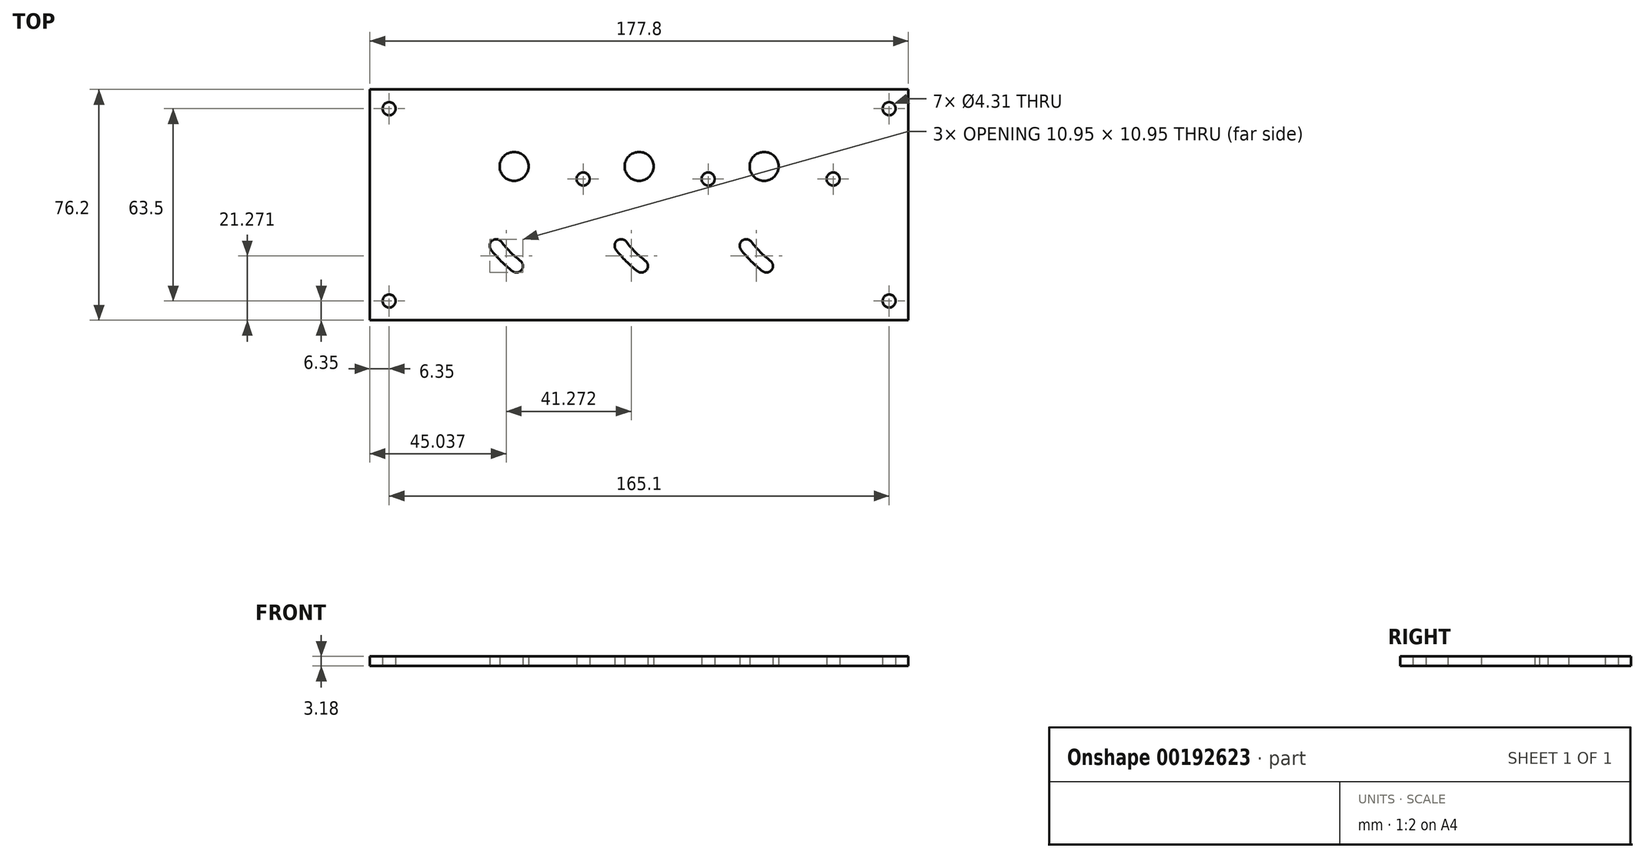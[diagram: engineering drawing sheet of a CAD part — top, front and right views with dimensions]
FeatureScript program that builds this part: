
annotation { "Feature Type Name" : "Feature", "Feature Type Description" : "" }
export const myFeature = defineFeature(function(context is Context, id is Id, definition is map)
    precondition{}
    {
        {
            var Q0;
            Q0=qCreatedBy(makeId("Top.planeOp"),FACE);
            var sketch = newSketch(context, id + "F0", { "sketchPlane" : qUnion([Q0])});
            skLineSegment(sketch, "E0.bottom", {"start": v(0, 76.2) * mm, "end": v(177.8, 76.2) * mm});
            skLineSegment(sketch, "E0.top", {"start": v(0, 0) * mm, "end": v(177.8, 0) * mm});
            skLineSegment(sketch, "E0.right", {"start": v(177.8, 76.2) * mm, "end": v(177.8, 0) * mm});
            skLineSegment(sketch, "E1", {"start": v(0, 76.2) * mm, "end": v(0, 0) * mm});
            skSolve(sketch);
        }
        {
            var Q0;
            Q0=qCreatedBy(makeId("Top.planeOp"),FACE);
            var sketch = newSketch(context, id + "F1", { "sketchPlane" : qUnion([Q0])});
            skPoint(sketch, "E2", {"position": v(130.18, 50.8) * mm});
            skPoint(sketch, "E3", {"position": v(88.9, 50.8) * mm});
            skPoint(sketch, "E4", {"position": v(47.63, 50.8) * mm});
            skLineSegment(sketch, "E5", {"start": v(47.63, 50.8) * mm, "end": v(61.1, 37.33) * mm});
            skLineSegment(sketch, "E6", {"start": v(44.82, 21.05) * mm, "end": v(70.41, 46.65) * mm});
            skLineSegment(sketch, "E7", {"start": v(88.9, 50.8) * mm, "end": v(102.37, 37.33) * mm});
            skLineSegment(sketch, "E8", {"start": v(86.09, 21.05) * mm, "end": v(111.69, 46.65) * mm});
            skLineSegment(sketch, "E9", {"start": v(130.18, 50.8) * mm, "end": v(143.65, 37.33) * mm});
            skLineSegment(sketch, "E10", {"start": v(127.37, 21.05) * mm, "end": v(152.96, 46.65) * mm});
            skArc(sketch, "E11", {"start": v(48.38, 17.93) * mm, "mid": v(44.82, 21.05) * mm, "end": v(41.7, 24.61) * mm});
            skLineSegment(sketch, "E12", {"start": v(48.38, 17.93) * mm, "end": v(70.41, 46.65) * mm});
            skLineSegment(sketch, "E13", {"start": v(41.7, 24.61) * mm, "end": v(70.41, 46.65) * mm});
            skArc(sketch, "E14", {"start": v(89.65, 17.93) * mm, "mid": v(86.09, 21.05) * mm, "end": v(82.97, 24.6) * mm});
            skLineSegment(sketch, "E15", {"start": v(111.69, 46.65) * mm, "end": v(82.97, 24.6) * mm});
            skLineSegment(sketch, "E16", {"start": v(89.65, 17.93) * mm, "end": v(111.69, 46.65) * mm});
            skCircle(sketch, "E17", {"center": v(61.1, 37.33) * mm, "radius": 12.7 * mm});
            skCircle(sketch, "E18", {"center": v(47.63, 50.8) * mm, "radius": 6.35 * mm});
            skCircle(sketch, "E19", {"center": v(88.9, 50.8) * mm, "radius": 6.35 * mm});
            skCircle(sketch, "E20", {"center": v(130.18, 50.8) * mm, "radius": 6.35 * mm});
            skCircle(sketch, "E21", {"center": v(102.37, 37.33) * mm, "radius": 12.7 * mm});
            skCircle(sketch, "E22", {"center": v(143.65, 37.33) * mm, "radius": 12.7 * mm});
            skArc(sketch, "E23", {"start": v(130.93, 17.93) * mm, "mid": v(127.37, 21.05) * mm, "end": v(124.25, 24.61) * mm});
            skLineSegment(sketch, "E24", {"start": v(124.25, 24.61) * mm, "end": v(152.96, 46.65) * mm});
            skLineSegment(sketch, "E25", {"start": v(130.93, 17.93) * mm, "end": v(152.96, 46.65) * mm});
            skLineSegment(sketch, "E26.bottom", {"start": v(6.35, 69.85) * mm, "end": v(171.45, 69.85) * mm});
            skLineSegment(sketch, "E26.top", {"start": v(6.35, 6.35) * mm, "end": v(171.45, 6.35) * mm});
            skLineSegment(sketch, "E26.left", {"start": v(6.35, 69.85) * mm, "end": v(6.35, 6.35) * mm});
            skLineSegment(sketch, "E26.right", {"start": v(171.45, 69.85) * mm, "end": v(171.45, 6.35) * mm});
            skSolve(sketch);
        }
        {
            var Q0;
            Q0=makeQuery(id+"F0.imprint","IMPRINT",FACE,{"disambiguationData":[TD([[makeQuery(id+"F0.imprint","IMPRINT",EDGE,{"derivedFrom":sQuery(id+"F0.wireOp",EDGE,"E0.bottom")}),-1.0]])]});
            var sketch = newSketch(context, id + "F2", { "sketchPlane" : qUnion([Q0])});
            skArc(sketch, "E27.JHZ.JHZ", {"start": v(48.38, 17.93) * mm, "mid": v(44.82, 21.05) * mm, "end": v(41.7, 24.61) * mm, "construction": true});
            skArc(sketch, "E27.0.startCap", {"start": v(49.69, 19.64) * mm, "mid": v(50.09, 16.62) * mm, "end": v(47.07, 16.22) * mm});
            skArc(sketch, "E27.0.endCap", {"start": v(39.99, 23.3) * mm, "mid": v(40.39, 26.32) * mm, "end": v(43.4, 25.92) * mm});
            skArc(sketch, "E27.0.left", {"start": v(47.07, 16.22) * mm, "mid": v(43.3, 19.53) * mm, "end": v(39.99, 23.3) * mm});
            skArc(sketch, "E27.0.right", {"start": v(49.69, 19.64) * mm, "mid": v(46.34, 22.57) * mm, "end": v(43.4, 25.92) * mm});
            skArc(sketch, "E28.JHl.JHl", {"start": v(89.65, 17.93) * mm, "mid": v(86.09, 21.05) * mm, "end": v(82.97, 24.6) * mm, "construction": true});
            skArc(sketch, "E28.0.startCap", {"start": v(90.96, 19.63) * mm, "mid": v(91.36, 16.62) * mm, "end": v(88.34, 16.22) * mm});
            skArc(sketch, "E28.0.endCap", {"start": v(81.26, 23.3) * mm, "mid": v(81.66, 26.32) * mm, "end": v(84.67, 25.92) * mm});
            skArc(sketch, "E28.0.left", {"start": v(88.34, 16.22) * mm, "mid": v(84.57, 19.53) * mm, "end": v(81.26, 23.3) * mm});
            skArc(sketch, "E28.0.right", {"start": v(90.96, 19.63) * mm, "mid": v(87.61, 22.57) * mm, "end": v(84.67, 25.92) * mm});
            skArc(sketch, "E29.KHJB.KHJB", {"start": v(130.93, 17.93) * mm, "mid": v(127.37, 21.05) * mm, "end": v(124.25, 24.61) * mm, "construction": true});
            skArc(sketch, "E29.0.startCap", {"start": v(132.24, 19.64) * mm, "mid": v(132.64, 16.62) * mm, "end": v(129.62, 16.22) * mm});
            skArc(sketch, "E29.0.endCap", {"start": v(122.54, 23.3) * mm, "mid": v(122.94, 26.32) * mm, "end": v(125.95, 25.92) * mm});
            skArc(sketch, "E29.0.left", {"start": v(129.62, 16.22) * mm, "mid": v(125.85, 19.53) * mm, "end": v(122.54, 23.3) * mm});
            skArc(sketch, "E29.0.right", {"start": v(132.24, 19.64) * mm, "mid": v(128.89, 22.57) * mm, "end": v(125.95, 25.92) * mm});
            skSolve(sketch);
        }
        {
            var Q0;
            Q0 = qSketchRegion(id + "F0", true);
            extrude(context, id + "F3", {"entities" : qUnion([Q0]), "depth" : 3.17 * mm});
        }
        {
            var Q0;
            Q0 = qSketchRegion(id + "F2", true);
            extrude(context, id + "F4", {"entities" : qUnion([Q0]), "operationType" : NewBodyOperationType.REMOVE, "endBound" : BoundingType.THROUGH_ALL, "depth" : 3.17 * mm});
        }
        {
            var Q0;
            Q0=sQuery(id+"F1.wireOp",VERTEX,"E6.end");
            var Q1;
            Q1=sQuery(id+"F1.wireOp",VERTEX,"E14.center");
            var Q2;
            Q2=sQuery(id+"F1.wireOp",VERTEX,"E23.center");
            var Q3;
            Q3=sQuery(id+"F1.wireOp",VERTEX,"E26.left.start");
            var Q4;
            Q4=sQuery(id+"F1.wireOp",VERTEX,"E26.left.end");
            var Q5;
            Q5=sQuery(id+"F1.wireOp",VERTEX,"E26.bottom.end");
            var Q6;
            Q6=sQuery(id+"F1.wireOp",VERTEX,"E26.top.end");
            var Q7;
            Q7=makeQuery(id+"F3.opExtrude","SWEPT_BODY",BODY,{"disambiguationData":[OSD([sQuery(id+"F0.wireOp",EDGE,"E0.bottom"),sQuery(id+"F0.wireOp",EDGE,"E0.top"),sQuery(id+"F0.wireOp",EDGE,"E0.left"),sQuery(id+"F0.wireOp",EDGE,"E0.right")])]});
            hole(context, id + "F5", {"style" : HoleStyle.SIMPLE, "endStyle" : HoleEndStyle.THROUGH, "oppositeDirection" : true, "holeDiameter" : 4.3 * mm, "locations" : qUnion([Q0, Q1, Q2, Q3, Q4, Q5, Q6]), "scope" : qUnion([Q7]), "isTappedThrough" : true});
        }
        {
            var Q0;
            Q0=sQuery(id+"F1.wireOp",VERTEX,"E5.start");
            var Q1;
            Q1=sQuery(id+"F1.wireOp",VERTEX,"E7.start");
            var Q2;
            Q2=sQuery(id+"F1.wireOp",VERTEX,"E2");
            var Q3;
            Q3=makeQuery(id+"F3.opExtrude","SWEPT_BODY",BODY,{"disambiguationData":[OSD([sQuery(id+"F0.wireOp",EDGE,"E0.bottom"),sQuery(id+"F0.wireOp",EDGE,"E0.top"),sQuery(id+"F0.wireOp",EDGE,"E0.left"),sQuery(id+"F0.wireOp",EDGE,"E0.right")])]});
            hole(context, id + "F6", {"style" : HoleStyle.SIMPLE, "endStyle" : HoleEndStyle.THROUGH, "oppositeDirection" : true, "holeDiameter" : 9.55 * mm, "locations" : qUnion([Q0, Q1, Q2]), "scope" : qUnion([Q3]), "isTappedThrough" : true});
        }
    });
